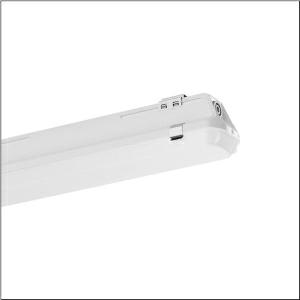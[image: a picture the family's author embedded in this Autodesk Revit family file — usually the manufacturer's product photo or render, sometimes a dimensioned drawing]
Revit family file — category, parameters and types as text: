
# Revit family: monsun_r__11_51fp109p440h_ab1f
name_source: partatom
category: Lighting Fixtures
units: mm (PartAtom-declared; Revit-internal decimal feet)

## family parameters
Cut with Voids When Loaded = No
Host = Face
Light Source = No
Part Type = Normal
Room Calculation Point = No
Round Connector Dimension = Use Diameter
Shared = No

## types (1)
- Monsun® 11 (1 x LED, 4120 lm, 22.9 W, 4000K)
    Apparent Load = 23 VA
    CIE Flux Codes = 47 77 93 94 100
    Color Rendering = 80
    Color Temperature = 4000K
    Default Elevation = 1800 mm
    Description = Monsun® 11, damp-proof luminaire, chain hanger, primary optical cover: enclosure, of PMMA, light emission: direct distribution, primary light characteristic: symmetric, installation type: suspended mounting, surface-mounted, horizontal mounting, vertical mounting, LED, rated luminous flux: 4.120lm, luminous efficacy: 180lm/W, light colour: 840, colour temperature: 4000K, control gear: ECG, with terminal, 3-pole, max. 2.5mm², mains connection: 220..240V, AC, 50/60Hz, start of lifetime: 23W, end of service life: 25W, luminaire housing, of glass-fibre reinforced polyester, uncoated, bright grey, incl. chain hanger, length: 1.590mm, width: 90mm, height: 88mm, clip for enclosure, of stainless steel (V2A), ceiling mounting element, of stainless steel (V2A), chain hanger, of stainless steel (V2A), protection rating (complete): IP66, insulation class (complete): insulation class I (protective earthing), certification: CE, ENEC, VDE, UKCA, protection symbol: D, impact resistance: IK04, permissible operating ambient temperature: -35..+40°C, standard: EN 50419, EN 60598-2-1, no direct snow, no direct sun, no direct rain, for indoor or canopied outdoor use, corresponds to IFS (International Featured Standards) requirements for safety and quality in the food industry, contact your sales advisor before using the luminaires in applications with unclear chemical exposure, large temperature fluctuations or condensation-forming humidity, LABS conformity tested according to VDMA 24364:2018-05, packaging unit: 1 piece
    Height = 89 mm
    Lamp = 1 x LED
    Lamp Light Flux = 4120 lm
    Lamp Power = 22.9 W
    Lamp count = 1
    Length = 1590 mm
    Luminous efficacy = 180 lm/W
    Manufacturer = Siteco
    ModVariant = No
    Model = 51FP109P440H
    Mounting Place = Ceiling
    Mounting Type = Surface mounted
    Number of Poles = 1
    OnlyDefault = Yes
    Power Factor = 1
    Product Name = Monsun® 11
    Product group = damp-proof luminaire
    ProductGroupID = 300
    Protection Class = Protection class I
    Protection Degree = IP 66
    RLX_Detail_Level = 1
    RLX_Emergency_Light_Flux = 0 lm
    RLX_Emergency_Type = 0
    RLX_Emergency_Type_DB = No
    RlxData = <blob elided: 88753 chars, md5=8c3bfb09>
    Socket = socket
    Standby Power = 0 W
    System Light Flux = 4120 lm
    System Power = 23 W
    Type Comments = Product without accessories
    Type Image = l_1319650.jpg
    URL = http://relux.com
    VarID = ---
    Voltage = 0 V
    Weight = 0.00 kg
    Width = 90 mm

## geometry (parser evidence)
native form markers: Blend x4, Sweep x12
no freeform markers — native parametric forms only
